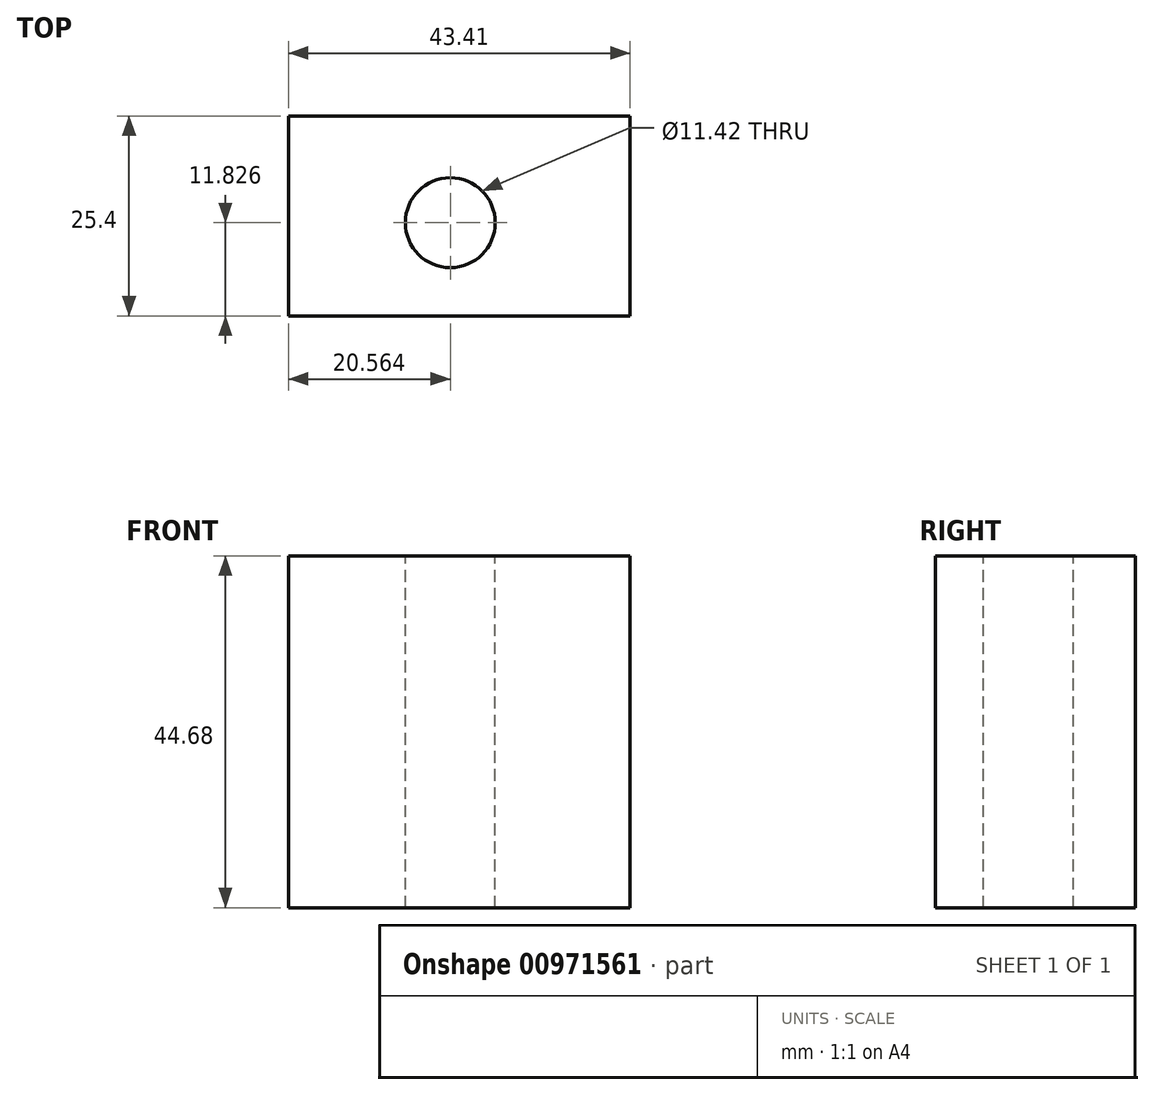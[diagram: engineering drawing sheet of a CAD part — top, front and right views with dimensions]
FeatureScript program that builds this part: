
annotation { "Feature Type Name" : "Feature", "Feature Type Description" : "" }
export const myFeature = defineFeature(function(context is Context, id is Id, definition is map)
    precondition{}
    {
        {
            var Q0;
            Q0=qCreatedBy(makeId("Front.planeOp"),FACE);
            var sketch = newSketch(context, id + "F0", { "sketchPlane" : qUnion([Q0])});
            skLineSegment(sketch, "E0.bottom", {"start": v(0, 0) * mm, "end": v(43.4, 0) * mm});
            skLineSegment(sketch, "E0.top", {"start": v(0, 44.68) * mm, "end": v(43.4, 44.68) * mm});
            skLineSegment(sketch, "E0.left", {"start": v(0, 0) * mm, "end": v(0, 44.68) * mm});
            skLineSegment(sketch, "E0.right", {"start": v(43.4, 0) * mm, "end": v(43.4, 44.68) * mm});
            skSolve(sketch);
        }
        {
            var Q0;
            Q0 = qSketchRegion(id + "F0", true);
            extrude(context, id + "F1", {"entities" : qUnion([Q0]), "depth" : 25.4 * mm, "offsetDistance" : 25.4 * mm});
        }
        {
            var Q0;
            Q0=makeQuery(id+"F1.opExtrude","SWEPT_FACE",FACE,{"disambiguationData":[OSD([sQuery(id+"F0.wireOp",EDGE,"E0.top")])]});
            var sketch = newSketch(context, id + "F2", { "sketchPlane" : qUnion([Q0])});
            skCircle(sketch, "E1", {"center": v(20.56, -13.57) * mm, "radius": 5.7 * mm});
            skSolve(sketch);
        }
        {
            var Q0;
            Q0=makeQuery(id+"F2.imprint","IMPRINT",FACE,{"disambiguationData":[TD([[makeQuery(id+"F2.imprint","IMPRINT",EDGE,{"derivedFrom":sQuery(id+"F2.wireOp",EDGE,"E1")}),1.0]])]});
            extrude(context, id + "F3", {"entities" : qUnion([Q0]), "operationType" : NewBodyOperationType.REMOVE, "endBound" : BoundingType.THROUGH_ALL, "oppositeDirection" : true, "depth" : 25.4 * mm, "offsetDistance" : 25.4 * mm});
        }
    });
